# Revit family: NBS_HeatraeSadia_IndrctHotWtrStrgCylndrsDblFeed_MEGAFLOCommercialIndirect
name_source: partatom
category: Plumbing Fixtures
revit_build: Autodesk Revit 2014 (Build: 20130709_2115(x64)
units: mm (PartAtom-declared; Revit-internal decimal feet)

## types (1)
- NBS_HeatraeSadia_IndrctHotWtrStrgCylndrsDblFeed_MEGAFLOCommercialIndirect
    Accessories = De-stratification loop kit (95:970:140), Pressure gauge (95:970:142), Temperature gauge (95:970:141)
    AssetType = Fixed
    BIMObjectName = NBS_HeatraeSadia_IndirectHotWaterStorageCylindersDoubleFeed_MEGAFLOCommercial-400i
    BottomInspectionHatchHeight = 456 mm
    CW Connection = Yes
    ColdWaterInletHeight = 396 mm
    Connections = All connections via BSP female parallel threaded pipe connections
    ControlHousingMaterial = NBS_Concept
    Description = Unvented indirect hot water cylinders
    DurationUnit = year
    EffectiveCapacity = 0 m³
    ElectricalDeviceNominalPower = 29400
    ErPRating = B
    FirstCurvatureRadius = 0 mm  [stored 0 ft]
    Fixing = Floor fixed
    FlowRate = ≤100 L/min
    HW Connection = Yes
    HasProtectiveEarth = No
    HeatUpTime = 21 minutes (minimum)
    Height = 1533 mm  [stored 5.02953 ft]
    IfcExportAs = IfcTankType
    IfcExportType = STORAGE
    ImmersionHeaterOptions = Single phase 6 kW element (95:970:155), Single phase 9 kW element (95:970:156), Three phase 12 kW element (95:970:144), Three phase 18 kW element (95:970:145), Three phase 24 kW element (95:970:146), Three phase 30 kW element (95:970:147), Three phase 36 kW element (95:970:148), Three phase 45 kW element (95:970:149)
    ManufacturerName = Heatrae Sadia
    ManufacturerURL = www.heatraesadia.com
    Material = Outer casing: Plastic-coated corrosion-proofed steel; Water container: Duplex stainless steel with internal air-gap system
    MaterialThickness = 0 mm  [stored 0 ft]
    ModelReference = MEGAFLO Commercial - 400i
    NBSCertification = http://www.nationalbimlibrary.com
    NBSDescription = Indirect hot water storage cylinders, double feed
    NBSReference = 90-15-35/310
    Name = IndirectHotWaterStorageCylindersDoubleFeed_MEGAFLOCommercial_HeatraeSadia
    NominalCapacity = 11.33 m³
    NominalCurrent = 0
    NominalDepth = 1535 mm
    NominalFrequencyRange = 50, 60
    NominalLengthOrDiameter = 872 mm
    NominalVoltage = 230, 240
    NominalWidthOrDiameter = 872 mm
    NumberOfPoles = 0
    OperatingWeight = 505
    OutletTemperatureRange = ≤80°C
    PatternType = Vertical cylinder
    PhaseAngle = 0.00°
    PrimaryCoilSurfaceArea = 2.0 m²
    PrimaryCoilType = 22 mm diameter stainless steel
    PrimaryFlowHeight = 711 mm
    PrimaryReturnHeight = 496 mm  [stored 1.6273 ft]
    ProductInformation = www.heatraesadia.com/docs/36006144_issue_2.pdf
    Radius = 425 mm  [stored 1.39436 ft]
    SafetyFeatures = Temperature and pressure relief valve factory set to operate at 10 bar and 90°C, thermostat and thermal cut-out
    SecondCurvatureRadius = 0 mm  [stored 0 ft]
    SecondaryReturnHeight = 906 mm
    SensorPocket1Height = 1096 mm  [stored 3.5958 ft]
    SensorPocket2Height = 941 mm
    SensorPocket3Height = 626 mm  [stored 2.05381 ft]
    Shape = Cylinder
    Size = 1535 x 872 x 872 mm
    StorageWaterHeaterMaterial = NBS_Concept
    SupplyPressureRange = 1.5-25.0 bar
    TemperaturePressureReliefValveHeight = 1096 mm  [stored 3.5958 ft]
    ThermalInsulation = 100 mm thick CFC/HCFC free (ODP zero) polyurethane
    TopInspectionHatchHeight = 811 mm
    Uniclass2 = 90-90-87/421
    Uniclass2015Description = Indirect hot water storage cylinders, double feed
    Uniclass2015Reference = Pr_60_50_20_21
    Uniclass2015Version = Products v1.1
    UsageCurrent = 0
    ValveMaterial = NBS_Concept
    Vent Connection = Yes
    Version = 1
    WarrantyDurationParts = 30
    WarrantyDurationUnit = year
    WarrantyStartDate = 1900-12-31T23:59:59
    Waste Connection = No
    Width = 850 mm

note: [stored X ft] marks values corroborated as IEEE doubles in the binary element streams (Revit-internal decimal feet)

## geometry (parser evidence)
native form markers: Sweep x8
no freeform markers — native parametric forms only
